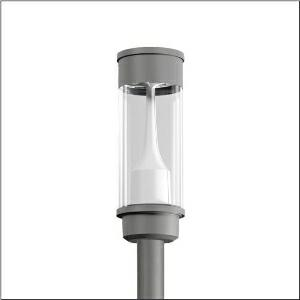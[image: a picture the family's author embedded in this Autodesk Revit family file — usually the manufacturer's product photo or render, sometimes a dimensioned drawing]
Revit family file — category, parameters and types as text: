
# Revit family: litepole_iq___p1_0a_5xa5415nf14h_8c95
name_source: partatom
category: Lighting Fixtures
units: mm (PartAtom-declared; Revit-internal decimal feet)

## family parameters
Cut with Voids When Loaded = No
Host = Face
Light Source = No
Part Type = Normal
Room Calculation Point = No
Round Connector Dimension = Use Diameter
Shared = No

## types (1)
- --- (1 x LED, 1510 lm, 11.8 W, 2700K)
    Apparent Load = 12 VA
    CIE Flux Codes = 32 61 90 93 100
    Color Rendering = 70
    Color Temperature = 2700K
    Default Elevation = 1800 mm
    Description = Litepole iQ, mast luminaire, Module 540 iQ-SR, primary light control with 3 zone facetted reflector, of plastic, silver coated, highly specular, structured, primary optical cover: cover, of PMMA, transparent, partly coated, light distribution: P1.0a, light emission: direct distribution, primary light characteristic: strongly asymmetric, installation type: post-top, LED, High Power LED, rated luminous flux: 1.510lm, luminous efficacy: 128lm/W, light colour: 727, colour temperature: 2700K, control gear: ECG iQ, control: optimised constant luminous flux control (CLO 2.0), Desk-Remote (wireless, voltage-free reading and setting of iQ features in the workshop via application-optimized NFC function/RFID function), Light-Fading, Smart-Wire, Night-Set, Lumen-Switch, Temp-Guard, Auto-Match, Street-Remote, presetting dimming logarithmic, with terminal, 6-pole, max. 2.5mm², mains connection: 220..240V, AC, 50/60Hz, start of lifetime: 12W, end of lifetime: 12W, reduction: 6W, luminaire housing, upper part, of glass-fibre reinforced polyester, coated, Siteco® metallic grey (DB 702S), diameter: 210mm, height: 590mm, spigot size: d x l = 76 x 70mm (post-top) | with reducer (optional accessory) 60 x 70mm, post-top mast mounting element, of diecast aluminium, coated, Siteco® metallic grey (DB 702S), Module 540 iQ-SR, traffic white (RAL 9016), equipment: standard, protection rating (complete): IP65, insulation class (complete): insulation class II (safety insulation), certification: CE, ENEC, VDE, packaging unit: 1 piece

Light Distribution: P1.0a
    Height = 590 mm
    Lamp = 1 x LED
    Lamp Light Flux = 1510 lm
    Lamp Power = 11.8 W
    Lamp count = 1
    Length = 220 mm
    Luminous efficacy = 128 lm/W
    Manufacturer = Siteco
    ModVariant = No
    Model = 5XA5415NF14H
    Number of Poles = 1
    OnlyDefault = Yes
    Power Factor = 1
    Product Name = Litepole iQ | P1.0a
    Product group = mast luminaire | pylon top
    ProductGroupID = 6100
    Protection Class = Protection class II
    Protection Degree = IP 65
    RLX_Detail_Level = 1
    RlxData = <blob elided: 63725 chars, md5=86766c0b>
    Socket = socket
    Standby Power = 0 W
    System Light Flux = 1510 lm
    System Power = 12 W
    Type Comments = factory setting: luminous flux: 100 % | dim-lin: 254 | 472 mA
    Type Image = l_1006025.jpg
    URL = http://relux.com
    VarID = @adj_062833
    Voltage = 0 V
    Weight = 0.00 kg
    Width = 0 mm  [stored 0 ft]

note: [stored X ft] marks values corroborated as IEEE doubles in the binary element streams (Revit-internal decimal feet)

## geometry (parser evidence)
native form markers: Blend x4, Sweep x12
no freeform markers — native parametric forms only
